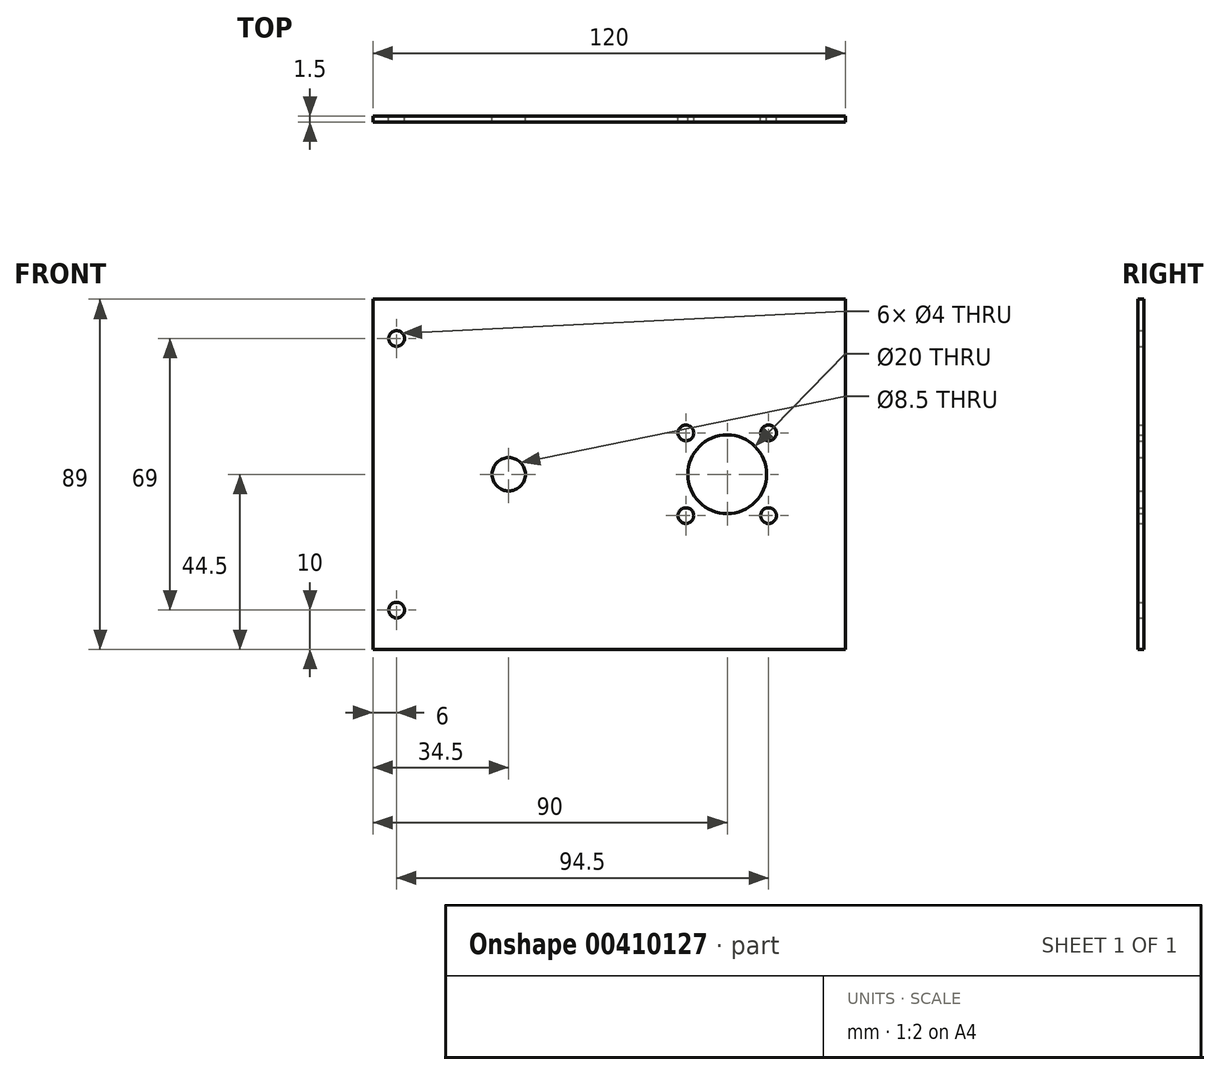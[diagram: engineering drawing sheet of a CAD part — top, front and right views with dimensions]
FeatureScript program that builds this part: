
annotation { "Feature Type Name" : "Feature", "Feature Type Description" : "" }
export const myFeature = defineFeature(function(context is Context, id is Id, definition is map)
    precondition{}
    {
        {
            var Q0;
            Q0=qCreatedBy(makeId("Front.planeOp"),FACE);
            var sketch = newSketch(context, id + "F0", { "sketchPlane" : qUnion([Q0])});
            skLineSegment(sketch, "E0.bottom", {"start": v(0, 0) * mm, "end": v(120, 0) * mm});
            skLineSegment(sketch, "E0.top", {"start": v(0, 89) * mm, "end": v(120, 89) * mm});
            skLineSegment(sketch, "E0.right", {"start": v(120, 0) * mm, "end": v(120, 89) * mm});
            skLineSegment(sketch, "E1", {"start": v(90, 89) * mm, "end": v(90, 0) * mm, "construction": true});
            skLineSegment(sketch, "E2.bottom", {"start": v(100.5, 34) * mm, "end": v(79.5, 34) * mm, "construction": true});
            skLineSegment(sketch, "E2.top", {"start": v(100.5, 55) * mm, "end": v(79.5, 55) * mm, "construction": true});
            skLineSegment(sketch, "E2.left", {"start": v(100.5, 34) * mm, "end": v(100.5, 55) * mm, "construction": true});
            skLineSegment(sketch, "E2.right", {"start": v(79.5, 34) * mm, "end": v(79.5, 55) * mm, "construction": true});
            skPoint(sketch, "E2.middle", {"position": v(90, 44.5) * mm});
            skCircle(sketch, "E3", {"center": v(100.5, 55) * mm, "radius": 2 * mm});
            skCircle(sketch, "E4", {"center": v(100.5, 34) * mm, "radius": 2 * mm});
            skCircle(sketch, "E5", {"center": v(79.5, 34) * mm, "radius": 2 * mm});
            skCircle(sketch, "E6", {"center": v(79.5, 55) * mm, "radius": 2 * mm});
            skCircle(sketch, "E7", {"center": v(90, 44.5) * mm, "radius": 10 * mm});
            skLineSegment(sketch, "E8", {"start": v(0, 89) * mm, "end": v(0, 0) * mm});
            skLineSegment(sketch, "E9", {"start": v(0, 0) * mm, "end": v(0, 0) * mm});
            skLineSegment(sketch, "E10", {"start": v(6, 89) * mm, "end": v(6, 0) * mm, "construction": true});
            skCircle(sketch, "E11", {"center": v(6, 79) * mm, "radius": 2 * mm});
            skCircle(sketch, "E12", {"center": v(6, 10) * mm, "radius": 2 * mm});
            skPoint(sketch, "E13", {"position": v(60, 89) * mm});
            skLineSegment(sketch, "E14", {"start": v(90, 44.5) * mm, "end": v(34.5, 44.5) * mm, "construction": true});
            skCircle(sketch, "E15", {"center": v(34.5, 44.5) * mm, "radius": 4.25 * mm});
            skSolve(sketch);
        }
        {
            var Q0;
            Q0 = qSketchRegion(id + "F0", true);
            extrude(context, id + "F1", {"entities" : qUnion([Q0]), "flatOperationType" : FlatOperationType.REMOVE, "offsetDistance" : 25 * mm, "depth" : 1.5 * mm, "domain" : OperationDomain.MODEL});
        }
    });
